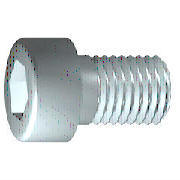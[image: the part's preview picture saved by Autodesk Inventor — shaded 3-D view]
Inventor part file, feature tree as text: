
AUTODESK INVENTOR PART (.ipt)
format: ipt  version: 2022 (Build 260153000, 153)  size: 195,584 bytes
history: native  units: mm (DEFAULTED — no unit token found)
features: sketch x2, extrude x1, plane x1, fillet x1
ambient origin geometry x7: Origin, YZ Plane, XY Plane, X Axis, Y Axis, Z Axis, Center Point
bodies: Solid1 (feature_tree), Body (feature_tree)
feature tree (5):
  extrude  "Slot"  Depth=4.0mm
  plane  "Work Plane1"
  fillet  "Fillet2"  Radius=4.0mm
  sketch  "Sketch1"  dims[d1=8.25mm d2=0.429515mm d3=4.0mm]
  sketch  "Sketch2"  dims[d4=2.0mm d5=60.0deg d6=4.0mm d7=4.0mm d8=3.464102mm d9=7.0mm d10=90.0deg d11=10.0mm d12=0.0mm d13=8.25mm d14=0.0mm d15=0.429415mm d16=0.429415mm d17=0.4mm d19=0.0mm d26=10.0mm d27=45.0deg d28=0.0mm d29=0.0mm d30=0.1mm]
